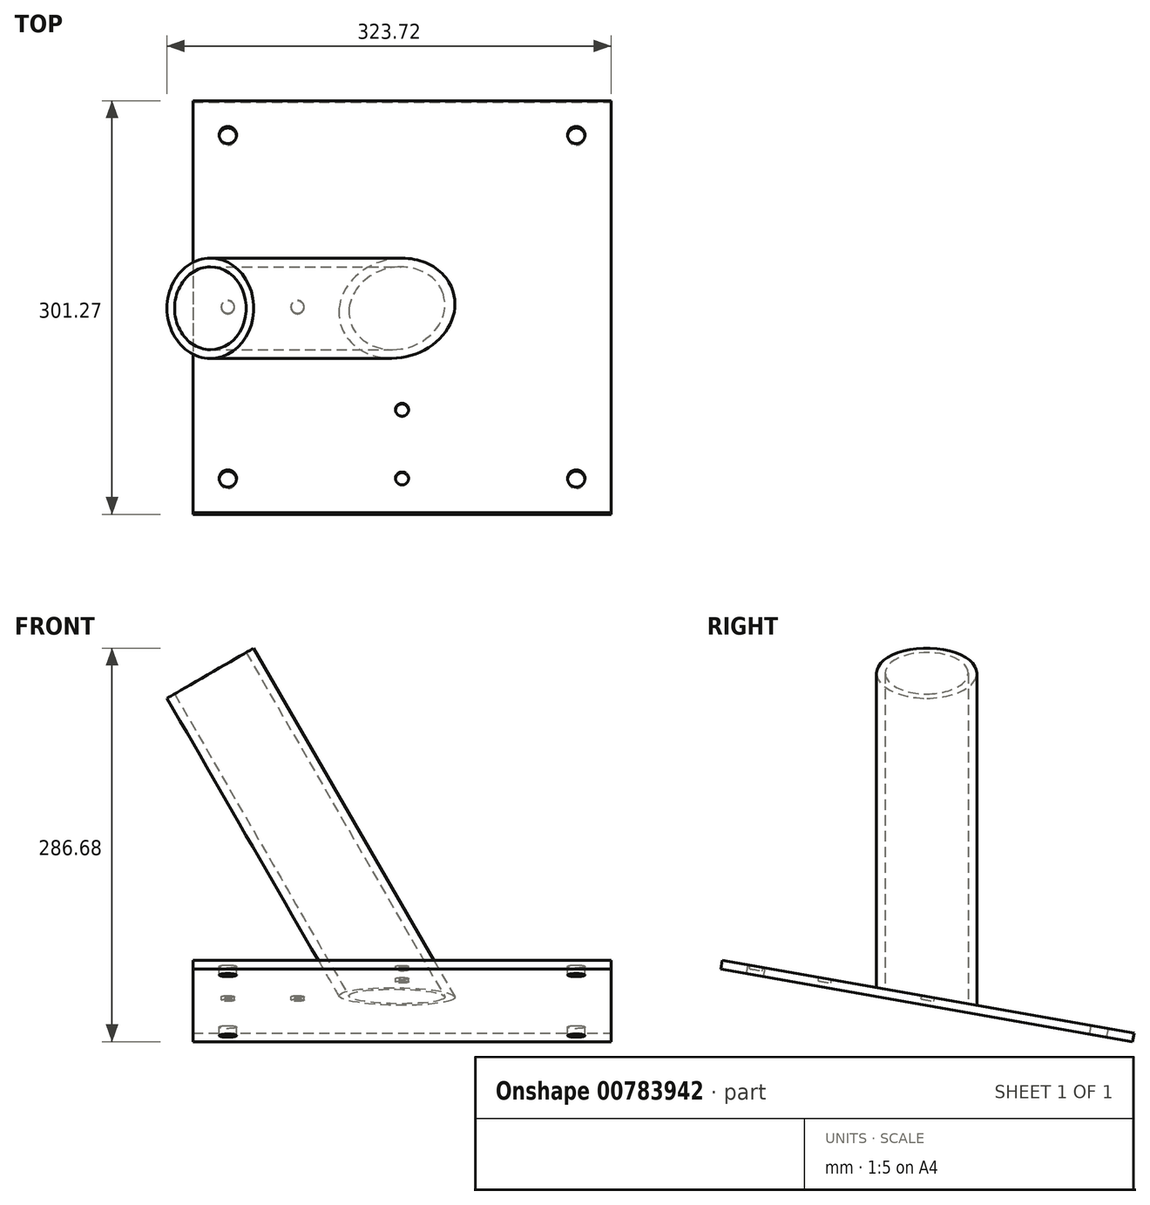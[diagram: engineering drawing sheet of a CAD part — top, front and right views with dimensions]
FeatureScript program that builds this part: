
annotation { "Feature Type Name" : "Feature", "Feature Type Description" : "" }
export const myFeature = defineFeature(function(context is Context, id is Id, definition is map)
    precondition{}
    {
        {
            var Q0;
            Q0=qCreatedBy(makeId("Top.planeOp"),FACE);
            var sketch = newSketch(context, id + "F0", { "sketchPlane" : qUnion([Q0])});
            skLineSegment(sketch, "E0.top", {"start": v(0, -25.4) * mm, "end": v(25.4, -25.4) * mm});
            skLineSegment(sketch, "E0.left", {"start": v(0, 0) * mm, "end": v(0, -25.4) * mm});
            skLineSegment(sketch, "E0.right", {"start": v(25.4, 0) * mm, "end": v(25.4, -25.4) * mm});
            skLineSegment(sketch, "E1", {"start": v(0, 0) * mm, "end": v(25.4, 0) * mm});
            skSolve(sketch);
        }
        {
            var Q0;
            Q0=sQuery(id+"F0.wireOp",EDGE,"E1");
            cPlane(context, id + "F1", {"entities" : qUnion([Q0]), "cplaneType" : CPlaneType.LINE_ANGLE, "offset" : 25.4 * mm, "angle" : 80 * degree, "width" : 152.4 * mm, "height" : 152.4 * mm});
        }
        {
            var Q0;
            Q0=qCreatedBy(id+"F1.planeOp",FACE);
            var sketch = newSketch(context, id + "F2", { "sketchPlane" : qUnion([Q0])});
            skLineSegment(sketch, "E2.bottom", {"start": v(-152.4, 152.4) * mm, "end": v(152.4, 152.4) * mm});
            skLineSegment(sketch, "E2.top", {"start": v(-152.4, -152.4) * mm, "end": v(152.4, -152.4) * mm});
            skLineSegment(sketch, "E2.left", {"start": v(-152.4, 152.4) * mm, "end": v(-152.4, -152.4) * mm});
            skLineSegment(sketch, "E2.right", {"start": v(152.4, 152.4) * mm, "end": v(152.4, -152.4) * mm});
            skSolve(sketch);
        }
        {
            var Q0;
            Q0=makeQuery(id+"F2.imprint","IMPRINT",FACE,{"disambiguationData":[TD([[makeQuery(id+"F2.imprint","IMPRINT",EDGE,{"derivedFrom":sQuery(id+"F2.wireOp",EDGE,"E2.bottom")}),-1.0]])]});
            extrude(context, id + "F3", {"entities" : qUnion([Q0]), "depth" : 6.35 * mm, "offsetDistance" : 25.4 * mm});
        }
        {
            var Q0;
            Q0=sQuery(id+"F0.wireOp",EDGE,"E0.right");
            cPlane(context, id + "F4", {"entities" : qUnion([Q0]), "cplaneType" : CPlaneType.LINE_ANGLE, "offset" : 25.4 * mm, "angle" : 330 * degree, "oppositeDirection" : true, "width" : 152.4 * mm, "height" : 152.4 * mm});
        }
        {
            var Q0;
            Q0=qCreatedBy(id+"F4.planeOp",FACE);
            var sketch = newSketch(context, id + "F5", { "sketchPlane" : qUnion([Q0])});
            skCircle(sketch, "E3", {"center": v(0, 0) * mm, "radius": 36.51 * mm});
            skCircle(sketch, "E4", {"center": v(0, 0) * mm, "radius": 30.16 * mm});
            skSolve(sketch);
        }
        {
            var Q0;
            Q0=makeQuery(id+"F5.imprint","IMPRINT",FACE,{"disambiguationData":[TD([[makeQuery(id+"F5.imprint","IMPRINT",EDGE,{"derivedFrom":sQuery(id+"F5.wireOp",EDGE,"E3")}),1.0]])]});
            extrude(context, id + "F6", {"entities" : qUnion([Q0]), "operationType" : NewBodyOperationType.ADD, "oppositeDirection" : true, "depth" : 292.1 * mm, "offsetDistance" : 25.4 * mm, "hasSecondDirection" : true, "secondDirectionOppositeDirection" : false, "secondDirectionDepth" : 12.7 * mm});
        }
        {
            var Q0;
            Q0=qCreatedBy(makeId("Right.planeOp"),FACE);
            var sketch = newSketch(context, id + "F7", { "sketchPlane" : qUnion([Q0])});
            skLineSegment(sketch, "E5", {"start": v(56.89, -10.03) * mm, "end": v(-39.13, 6.9) * mm});
            skLineSegment(sketch, "E6", {"start": v(-39.13, 6.9) * mm, "end": v(-39.13, -43.9) * mm});
            skLineSegment(sketch, "E7", {"start": v(-39.13, -43.9) * mm, "end": v(56.89, -43.9) * mm});
            skLineSegment(sketch, "E8", {"start": v(56.89, -43.9) * mm, "end": v(56.89, -10.03) * mm});
            skSolve(sketch);
        }
        {
            var Q0;
            Q0=makeQuery(id+"F7.imprint","IMPRINT",FACE,{"disambiguationData":[TD([[makeQuery(id+"F7.imprint","IMPRINT",EDGE,{"derivedFrom":sQuery(id+"F7.wireOp",EDGE,"E5")}),1.0]])]});
            extrude(context, id + "F8", {"entities" : qUnion([Q0]), "operationType" : NewBodyOperationType.REMOVE, "oppositeDirection" : true, "depth" : 50.8 * mm, "offsetDistance" : 25.4 * mm, "hasSecondDirection" : true, "secondDirectionOppositeDirection" : false, "secondDirectionDepth" : 50.8 * mm});
        }
        {
            var Q0;
            {var subQ0=sQuery(id+"F2.wireOp",EDGE,"E2.left");var subQ1=sQuery(id+"F2.wireOp",EDGE,"E2.top");var subQ2=sQuery(id+"F2.wireOp",EDGE,"E2.right");var subQ3=sQuery(id+"F2.wireOp",EDGE,"E2.bottom");Q0=makeQuery(id+"F6.boolean.opBoolean","SPLIT",FACE,{"disambiguationData":[TD([makeQuery(id+"F3.opExtrude","SWEPT_FACE",FACE,{"disambiguationData":[OSD([subQ3])]})])],"derivedFrom":makeQuery(id+"F3.opExtrude","CAP_FACE",FACE,{"disambiguationData":[OSD([subQ3,subQ1,subQ0,subQ2])],"isStart":false})});}
            var sketch = newSketch(context, id + "F9", { "sketchPlane" : qUnion([Q0])});
            skCircle(sketch, "E9", {"center": v(0, -127) * mm, "radius": 4.76 * mm});
            skCircle(sketch, "E10", {"center": v(0, -76.2) * mm, "radius": 4.76 * mm});
            skCircle(sketch, "E11", {"center": v(-127, 0) * mm, "radius": 4.76 * mm});
            skCircle(sketch, "E12", {"center": v(-76.2, 0) * mm, "radius": 4.76 * mm});
            skSolve(sketch);
        }
        {
            var Q0;
            Q0=makeQuery(id+"F9.imprint","IMPRINT",FACE,{"disambiguationData":[TD([[makeQuery(id+"F9.imprint","IMPRINT",EDGE,{"derivedFrom":sQuery(id+"F9.wireOp",EDGE,"E10")}),1.0]])]});
            var Q1;
            Q1=makeQuery(id+"F9.imprint","IMPRINT",FACE,{"disambiguationData":[TD([[makeQuery(id+"F9.imprint","IMPRINT",EDGE,{"derivedFrom":sQuery(id+"F9.wireOp",EDGE,"E9")}),1.0]])]});
            var Q2;
            Q2=makeQuery(id+"F9.imprint","IMPRINT",FACE,{"disambiguationData":[TD([[makeQuery(id+"F9.imprint","IMPRINT",EDGE,{"derivedFrom":sQuery(id+"F9.wireOp",EDGE,"E11")}),1.0]])]});
            var Q3;
            Q3=makeQuery(id+"F9.imprint","IMPRINT",FACE,{"disambiguationData":[TD([[makeQuery(id+"F9.imprint","IMPRINT",EDGE,{"derivedFrom":sQuery(id+"F9.wireOp",EDGE,"E12")}),1.0]])]});
            extrude(context, id + "F10", {"entities" : qUnion([Q0, Q1, Q2, Q3]), "operationType" : NewBodyOperationType.REMOVE, "oppositeDirection" : true, "depth" : 2.54 * mm, "offsetDistance" : 25.4 * mm});
        }
        {
            var Q0;
            {var subQ0=sQuery(id+"F2.wireOp",EDGE,"E2.left");var subQ1=sQuery(id+"F2.wireOp",EDGE,"E2.top");var subQ2=sQuery(id+"F2.wireOp",EDGE,"E2.right");var subQ3=sQuery(id+"F2.wireOp",EDGE,"E2.bottom");Q0=makeQuery(id+"F6.boolean.opBoolean","SPLIT",FACE,{"disambiguationData":[TD([makeQuery(id+"F3.opExtrude","SWEPT_FACE",FACE,{"disambiguationData":[OSD([subQ3])]})])],"derivedFrom":makeQuery(id+"F3.opExtrude","CAP_FACE",FACE,{"disambiguationData":[OSD([subQ3,subQ1,subQ0,subQ2])],"isStart":false})});}
            var sketch = newSketch(context, id + "F11", { "sketchPlane" : qUnion([Q0])});
            skCircle(sketch, "E13", {"center": v(-127, 127) * mm, "radius": 6.35 * mm});
            skCircle(sketch, "E14", {"center": v(127, 127) * mm, "radius": 6.35 * mm});
            skCircle(sketch, "E15", {"center": v(127, -127) * mm, "radius": 6.35 * mm});
            skCircle(sketch, "E16", {"center": v(-127, -127) * mm, "radius": 6.35 * mm});
            skSolve(sketch);
        }
        {
            var Q0;
            Q0=makeQuery(id+"F11.imprint","IMPRINT",FACE,{"disambiguationData":[TD([[makeQuery(id+"F11.imprint","IMPRINT",EDGE,{"derivedFrom":sQuery(id+"F11.wireOp",EDGE,"E14")}),1.0]])]});
            var Q1;
            Q1=makeQuery(id+"F11.imprint","IMPRINT",FACE,{"disambiguationData":[TD([[makeQuery(id+"F11.imprint","IMPRINT",EDGE,{"derivedFrom":sQuery(id+"F11.wireOp",EDGE,"E15")}),1.0]])]});
            var Q2;
            Q2=makeQuery(id+"F11.imprint","IMPRINT",FACE,{"disambiguationData":[TD([[makeQuery(id+"F11.imprint","IMPRINT",EDGE,{"derivedFrom":sQuery(id+"F11.wireOp",EDGE,"E16")}),1.0]])]});
            var Q3;
            Q3=makeQuery(id+"F11.imprint","IMPRINT",FACE,{"disambiguationData":[TD([[makeQuery(id+"F11.imprint","IMPRINT",EDGE,{"derivedFrom":sQuery(id+"F11.wireOp",EDGE,"E13")}),1.0]])]});
            extrude(context, id + "F12", {"entities" : qUnion([Q0, Q1, Q2, Q3]), "operationType" : NewBodyOperationType.REMOVE, "oppositeDirection" : true, "depth" : 25.4 * mm, "offsetDistance" : 25.4 * mm});
        }
    });
